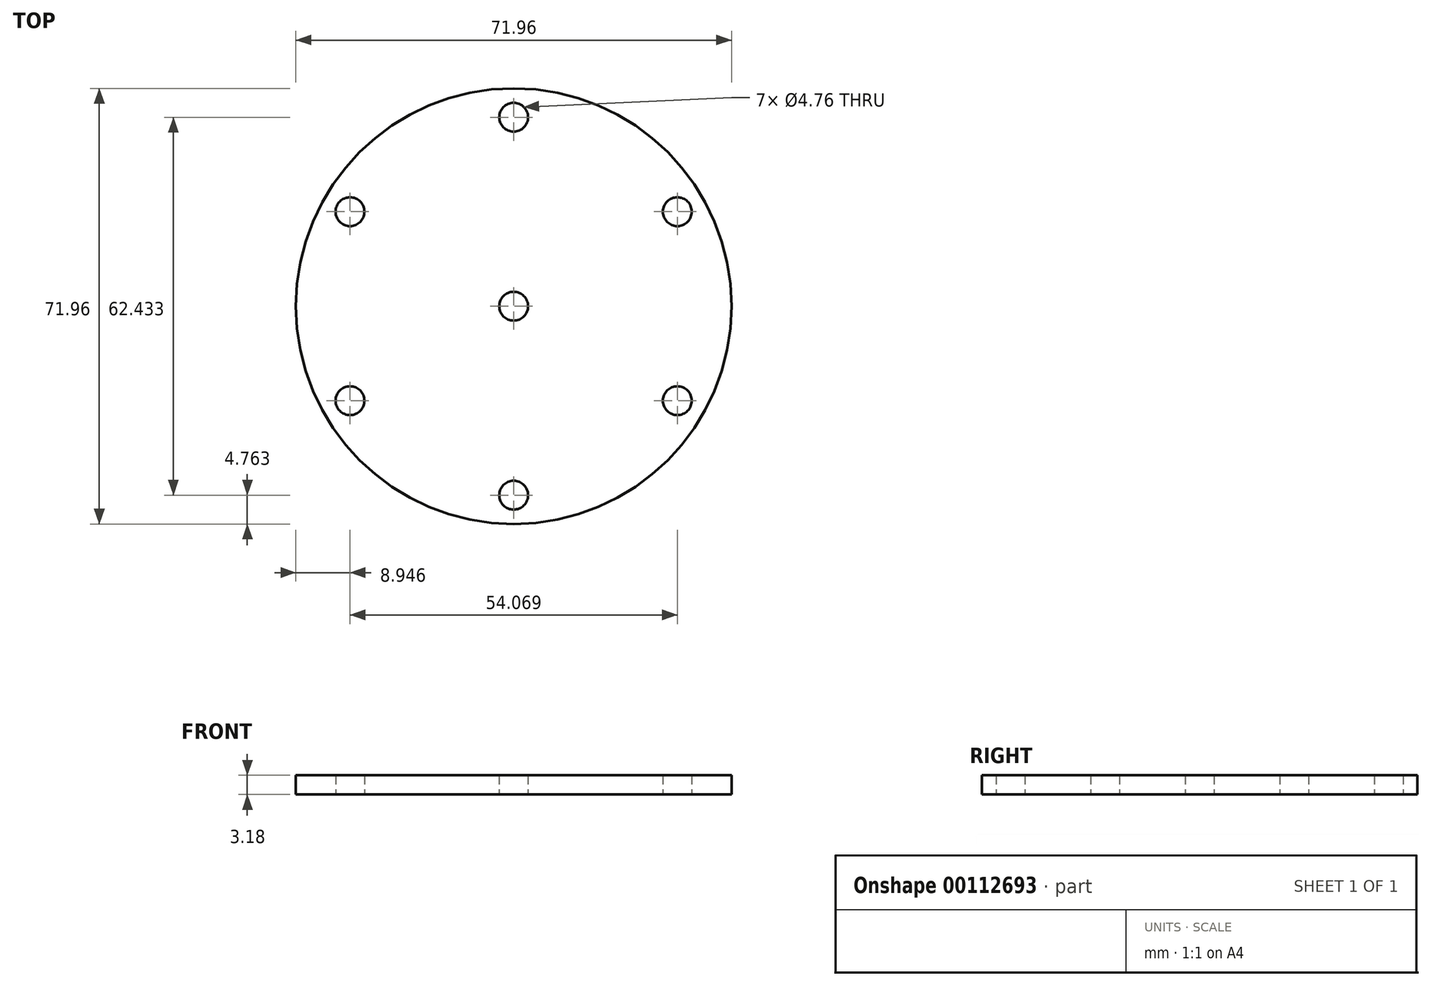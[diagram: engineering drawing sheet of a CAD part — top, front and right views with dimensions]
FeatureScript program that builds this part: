
annotation { "Feature Type Name" : "Feature", "Feature Type Description" : "" }
export const myFeature = defineFeature(function(context is Context, id is Id, definition is map)
    precondition{}
    {
        {
            var Q0;
            Q0=qCreatedBy(makeId("Top.planeOp"),FACE);
            var sketch = newSketch(context, id + "F0", { "sketchPlane" : qUnion([Q0])});
            skCircle(sketch, "E0", {"center": v(0, 0) * mm, "radius": 35.98 * mm});
            skSolve(sketch);
        }
        {
            var Q0;
            Q0=qSketchRegion(id+"F0",true);
            extrude(context, id + "F1", {"entities" : qUnion([Q0]), "depth" : 3.17 * mm});
        }
        {
            var Q0;
            Q0=makeQuery(id+"F1.opExtrude","CAP_FACE",FACE,{"disambiguationData":[OSD([sQuery(id+"F0.wireOp",EDGE,"E0")])],"isStart":true});
            var sketch = newSketch(context, id + "F2", { "sketchPlane" : qUnion([Q0])});
            skCircle(sketch, "E1", {"center": v(-27.03, -15.6) * mm, "radius": 4.76 * mm, "construction": true});
            skCircle(sketch, "E2.cCircle", {"center": v(0, 0) * mm, "radius": 27.03 * mm, "construction": true});
            skLineSegment(sketch, "E2.0", {"start": v(27.03, 15.6) * mm, "end": v(27.03, -15.6) * mm, "construction": true});
            skLineSegment(sketch, "E2.1", {"start": v(27.03, -15.6) * mm, "end": v(0, -31.22) * mm, "construction": true});
            skLineSegment(sketch, "E2.2", {"start": v(0, -31.22) * mm, "end": v(-27.03, -15.6) * mm, "construction": true});
            skLineSegment(sketch, "E2.3", {"start": v(-27.03, -15.6) * mm, "end": v(-27.03, 15.6) * mm, "construction": true});
            skLineSegment(sketch, "E2.4", {"start": v(-27.03, 15.6) * mm, "end": v(0, 31.22) * mm, "construction": true});
            skLineSegment(sketch, "E2.5", {"start": v(0, 31.22) * mm, "end": v(27.03, 15.6) * mm, "construction": true});
            skPoint(sketch, "E2.0.midPoint", {"position": v(27.03, 0) * mm});
            skCircle(sketch, "E3", {"center": v(-27.03, -15.6) * mm, "radius": 2.38 * mm});
            skCircle(sketch, "E4", {"center": v(-27.03, 15.6) * mm, "radius": 2.38 * mm});
            skCircle(sketch, "E5", {"center": v(0, 31.22) * mm, "radius": 2.38 * mm});
            skCircle(sketch, "E6", {"center": v(27.03, 15.6) * mm, "radius": 2.38 * mm});
            skCircle(sketch, "E7", {"center": v(27.03, -15.6) * mm, "radius": 2.38 * mm});
            skCircle(sketch, "E8", {"center": v(0, -31.22) * mm, "radius": 2.38 * mm});
            skCircle(sketch, "E9", {"center": v(0, 0) * mm, "radius": 2.38 * mm});
            skSolve(sketch);
        }
        {
            var Q0;
            Q0=qSketchRegion(id+"F2",true);
            extrude(context, id + "F3", {"entities" : qUnion([Q0]), "operationType" : NewBodyOperationType.REMOVE, "oppositeDirection" : true, "depth" : 12.7 * mm});
        }
    });
